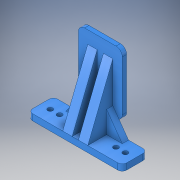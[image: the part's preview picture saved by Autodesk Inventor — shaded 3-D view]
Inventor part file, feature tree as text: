
AUTODESK INVENTOR PART (.ipt)
format: ipt  version: 2019 (Build 230136000, 136)  size: 249,856 bytes
history: native  units: mm
features: projected_geometry x13, extrude x6, sketch x6, fillet x2, plane x1
ambient origin geometry x8: Origin, YZ Plane, XZ Plane, XY Plane, X Axis, Y Axis, Z Axis, Center Point
bodies: Solid1 (feature_tree)
feature tree (28):
  extrude  "Extrusion1"  Depth=100.0mm
  fillet  "Fillet1"  Radius=7.0mm
  plane  "Work Plane1"
  extrude  "Extrusion2"  [1 undecoded]
  extrude  "Extrusion3"  Depth=40.0mm
  fillet  "Fillet2"  Radius=100.0mm
  extrude  "Extrusion4"  Depth=55.0mm
  extrude  "Extrusion5"  Depth=10.0mm TaperAngle=0.0deg
  extrude  "Extrusion6"  Depth=20.0mm
  sketch  "Sketch1"  dims[d0=70.0mm d1=100.0mm d2=7.0mm d3=0.0mm]
  sketch  "Sketch2"  dims[d4=10.0mm d5=-15.0mm]
  projected_geometry  "Projected Loop1"
  projected_geometry  "Projected Loop2"
  projected_geometry  "Projected Loop3"
  sketch  "Sketch3"  dims[d6=50.0mm d8=40.0mm d9=100.0mm]
  projected_geometry  "Projected Loop4"
  projected_geometry  "Projected Loop5"
  projected_geometry  "Projected Loop6"
  projected_geometry  "Projected Loop7"
  sketch  "Sketch5"  dims[d10=40.0mm d11=0.0mm d12=55.0mm]
  projected_geometry  "Projected Loop9"
  sketch  "Sketch7"  dims[d13=150.0mm d14=10.0mm d15=0.0mm]
  projected_geometry  "Projected Loop11"
  sketch  "Sketch8"  dims[d16=7.0mm d17=20.0mm d18=40.0mm d23=8.0mm d24=8.0mm d25=15.0mm d26=15.0mm d27=20.0mm d28=0.0mm d29=8.0mm d30=8.0mm d31=15.0mm d32=15.0mm d33=10.0mm d34=40.0mm d35=0.0mm d36=25.0mm d37=35.0mm d38=10.0mm d39=0.0mm]
  projected_geometry  "Projected Loop12"
  projected_geometry  "Projected Loop13"
  projected_geometry  "Projected Loop14"
  projected_geometry  "Projected Loop15"
note: 1 required parameter value undecoded (feature->parameter linkage not recoverable at this tier; creation-order binding heuristic only, values carry confidence <= 0.55)
